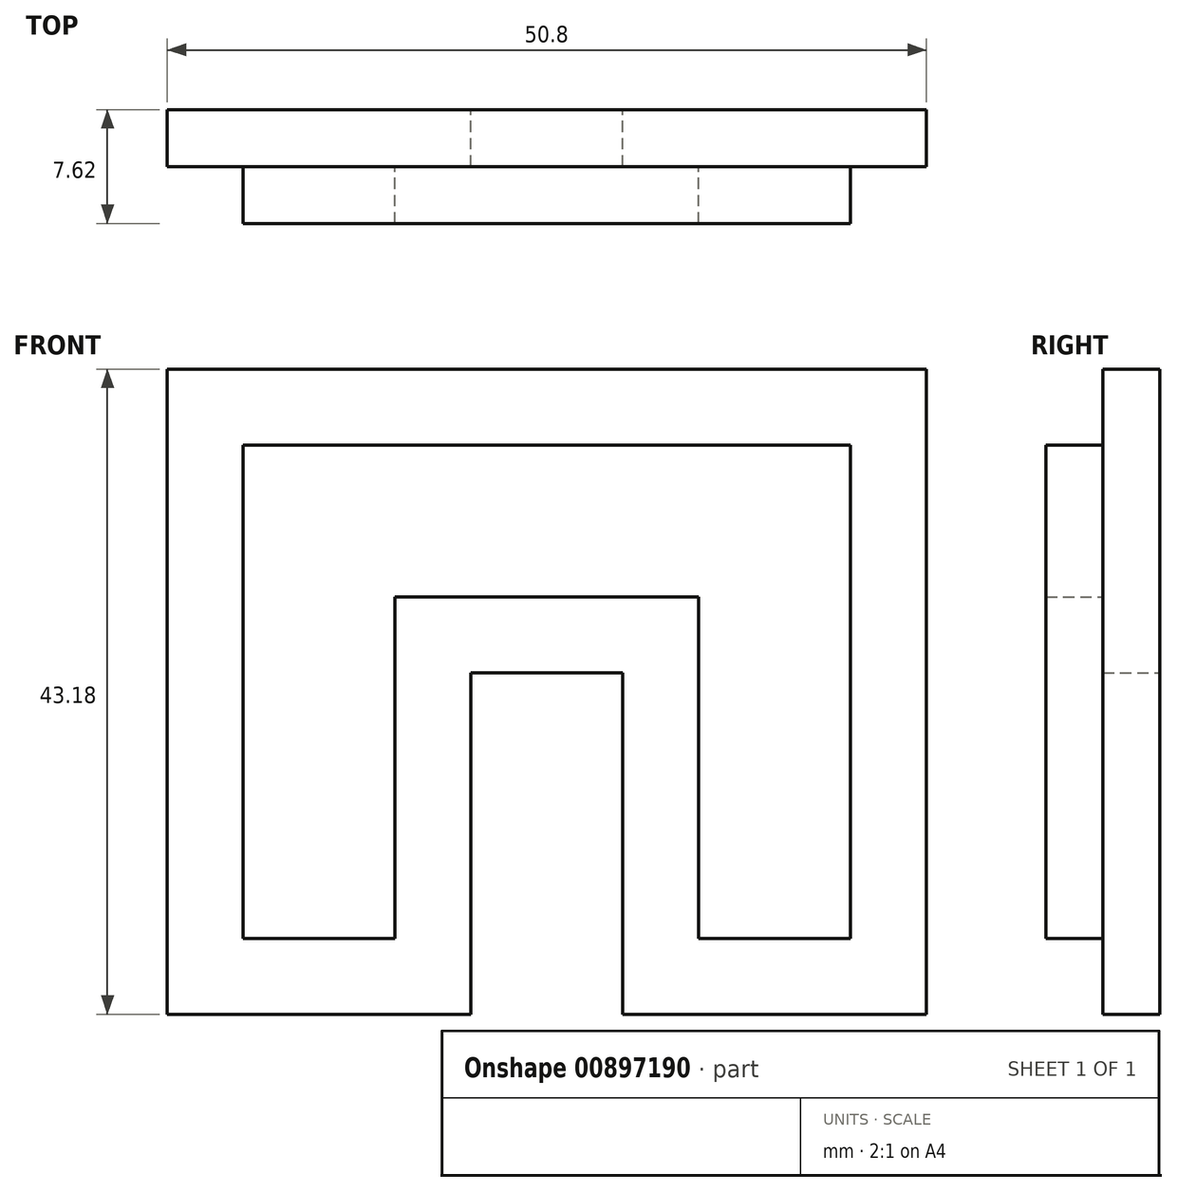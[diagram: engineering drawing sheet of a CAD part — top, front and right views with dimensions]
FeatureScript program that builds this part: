
annotation { "Feature Type Name" : "Feature", "Feature Type Description" : "" }
export const myFeature = defineFeature(function(context is Context, id is Id, definition is map)
    precondition{}
    {
        {
            var Q0;
            Q0=qCreatedBy(makeId("Front.planeOp"),FACE);
            var sketch = newSketch(context, id + "F0", { "sketchPlane" : qUnion([Q0])});
            skLineSegment(sketch, "E0.bottom", {"start": v(-25.4, 19.05) * mm, "end": v(25.4, 19.05) * mm});
            skLineSegment(sketch, "E0.top", {"start": v(-25.4, -19.05) * mm, "end": v(-5.08, -19.05) * mm});
            skLineSegment(sketch, "E0.left", {"start": v(-25.4, 19.05) * mm, "end": v(-25.4, -19.05) * mm});
            skLineSegment(sketch, "E0.right", {"start": v(25.4, 19.05) * mm, "end": v(25.4, -19.05) * mm});
            skPoint(sketch, "E0.middle", {"position": v(0, 0) * mm});
            skLineSegment(sketch, "E1", {"start": v(-20.32, -19.05) * mm, "end": v(-20.32, 13.97) * mm});
            skLineSegment(sketch, "E2", {"start": v(-20.32, 13.97) * mm, "end": v(20.32, 13.97) * mm});
            skLineSegment(sketch, "E3", {"start": v(20.32, 13.97) * mm, "end": v(20.32, -19.05) * mm});
            skLineSegment(sketch, "E4", {"start": v(-10.16, -19.05) * mm, "end": v(-10.16, 3.81) * mm});
            skLineSegment(sketch, "E5", {"start": v(-10.16, 3.81) * mm, "end": v(10.16, 3.81) * mm});
            skLineSegment(sketch, "E6", {"start": v(10.16, 3.81) * mm, "end": v(10.16, -19.05) * mm});
            skLineSegment(sketch, "E7", {"start": v(-5.08, -19.05) * mm, "end": v(-5.08, -1.27) * mm});
            skLineSegment(sketch, "E8", {"start": v(-5.08, -1.27) * mm, "end": v(5.08, -1.27) * mm});
            skLineSegment(sketch, "E9", {"start": v(5.08, -1.27) * mm, "end": v(5.08, -19.05) * mm});
            skLineSegment(sketch, "E10.trimOffspring", {"start": v(5.08, -19.05) * mm, "end": v(25.4, -19.05) * mm});
            skLineSegment(sketch, "E11", {"start": v(-25.4, -19.05) * mm, "end": v(-25.4, -24.13) * mm});
            skLineSegment(sketch, "E12", {"start": v(-25.4, -24.13) * mm, "end": v(-5.08, -24.13) * mm});
            skLineSegment(sketch, "E13", {"start": v(-5.08, -24.13) * mm, "end": v(-5.08, -19.05) * mm});
            skLineSegment(sketch, "E14", {"start": v(5.08, -19.05) * mm, "end": v(5.08, -24.13) * mm});
            skLineSegment(sketch, "E15", {"start": v(5.08, -24.13) * mm, "end": v(25.4, -24.13) * mm});
            skLineSegment(sketch, "E16", {"start": v(25.4, -24.13) * mm, "end": v(25.4, -19.05) * mm});
            skSolve(sketch);
        }
        {
            var Q0;
            {var subQ1=sQuery(id+"F0.wireOp",EDGE,"E1");Q0=makeQuery(id+"F0.imprint","IMPRINT",FACE,{"disambiguationData":[TD([[makeQuery(id+"F0.imprint","IMPRINT",EDGE,{"derivedFrom":subQ1}),-1.0]])]});}
            extrude(context, id + "F1", {"entities" : qUnion([Q0]), "depth" : 7.62 * mm, "offsetDistance" : 25.4 * mm});
        }
        {
            var Q0;
            Q0=makeQuery(id+"F0.imprint","IMPRINT",FACE,{"disambiguationData":[TD([[makeQuery(id+"F0.imprint","IMPRINT",EDGE,{"derivedFrom":sQuery(id+"F0.wireOp",EDGE,"E0.bottom")}),-1.0]])]});
            var Q1;
            {var subQ1=sQuery(id+"F0.wireOp",EDGE,"E4");Q1=makeQuery(id+"F0.imprint","IMPRINT",FACE,{"disambiguationData":[TD([[makeQuery(id+"F0.imprint","IMPRINT",EDGE,{"derivedFrom":subQ1}),-1.0]])]});}
            var Q2;
            {var subQ0=sQuery(id+"F0.wireOp",EDGE,"E11");Q2=makeQuery(id+"F0.imprint","IMPRINT",FACE,{"disambiguationData":[TD([[makeQuery(id+"F0.imprint","IMPRINT",EDGE,{"derivedFrom":subQ0}),1.0]])]});}
            var Q3;
            {var subQ3=sQuery(id+"F0.wireOp",EDGE,"E14");Q3=makeQuery(id+"F0.imprint","IMPRINT",FACE,{"disambiguationData":[TD([[makeQuery(id+"F0.imprint","IMPRINT",EDGE,{"derivedFrom":subQ3}),1.0]])]});}
            extrude(context, id + "F2", {"entities" : qUnion([Q0, Q1, Q2, Q3]), "operationType" : NewBodyOperationType.ADD, "depth" : 3.8 * mm, "offsetDistance" : 25.4 * mm});
        }
    });
